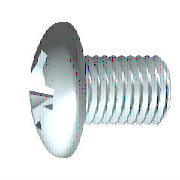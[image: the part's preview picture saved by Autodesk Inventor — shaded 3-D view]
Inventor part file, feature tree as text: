
AUTODESK INVENTOR PART (.ipt)
format: ipt  version: 2013 (Build 170138000, 138)  size: 302,080 bytes
history: native  units: mm (DEFAULTED — no unit token found)
features: other x2, extrude x2, plane x1
ambient origin geometry x7: Origin, YZ Plane, XZ Plane, X Axis, Y Axis, Z Axis, Center Point
bodies: Solid1 (feature_tree), Body (feature_tree)
feature tree (5):
  other  "IDS_WORKPLANE{1}"
  extrude  "Slot"  Depth=2.0mm
  other  "Cut"
  extrude  "Star Cut"  Depth=1.4mm
  plane  "Work Plane3"
